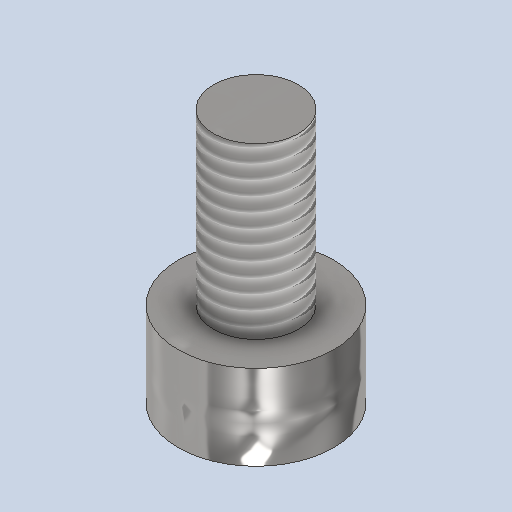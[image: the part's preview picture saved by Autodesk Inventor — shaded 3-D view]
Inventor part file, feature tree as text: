
AUTODESK INVENTOR PART (.ipt)
format: ipt  version: 2024.2 (Build 282272000, 272)  size: 185,344 bytes
history: native  units: mm
features: sketch x2, revolve x1, thread x1, extrude x1
ambient origin geometry x8: Origin, YZ Plane, XZ Plane, XY Plane, X Axis, Y Axis, Z Axis, Center Point
bodies: Solid1 (feature_tree)
feature tree (5):
  revolve  "Revolution1"  [1 undecoded]
  thread  "Thread1"  [1 undecoded]
  extrude  "Extrusion1"  [1 undecoded]
  sketch  "Sketch1"  dims[d4=90.0deg d5=6.0mm d6=0.0mm d0=0.0mm]
  sketch  "Sketch2"
note: 3 required parameter values undecoded (feature->parameter linkage not recoverable at this tier; creation-order binding heuristic only, values carry confidence <= 0.55)